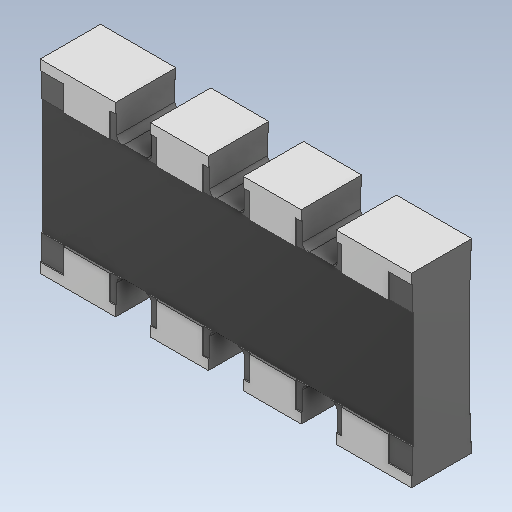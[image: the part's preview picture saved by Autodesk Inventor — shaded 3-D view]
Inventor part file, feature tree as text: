
AUTODESK INVENTOR PART (.ipt)
format: ipt  version: 2020 (Build 240168000, 168)  size: 228,352 bytes
history: native  units: mm
features: other x1, mirror x1
ambient origin geometry x8: Origin, YZ Plane, XZ Plane, XY Plane, X Axis, Y Axis, Z Axis, Center Point
bodies: Body1 (feature_tree)
feature tree (2):
  other  "Твердое тело1"
  mirror  "Mirror2"
